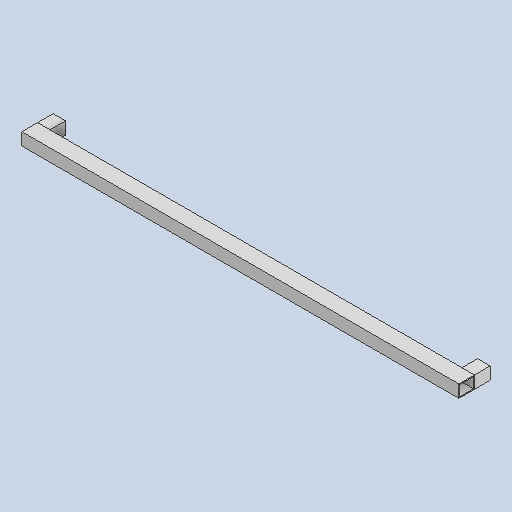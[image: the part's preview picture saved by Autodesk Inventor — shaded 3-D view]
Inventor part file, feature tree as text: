
AUTODESK INVENTOR PART (.ipt)
format: ipt  version: 2025 (Build 290162000, 162)  size: 112,640 bytes
history: native  units: mm
features: extrude x2, shell x2
ambient origin geometry x8: Origin, YZ Plane, XZ Plane, XY Plane, X Axis, Y Axis, Z Axis, Center Point
bodies: Solid1 (feature_tree), Solid2 (feature_tree)
feature tree (4):
  extrude  "Extrusion1"  Depth=1400.0mm
  extrude  "Extrusion2"  Depth=50.0mm
  shell  "Shell1"  Thickness=40.0mm
  shell  "Shell2"  Thickness=50.0mm
